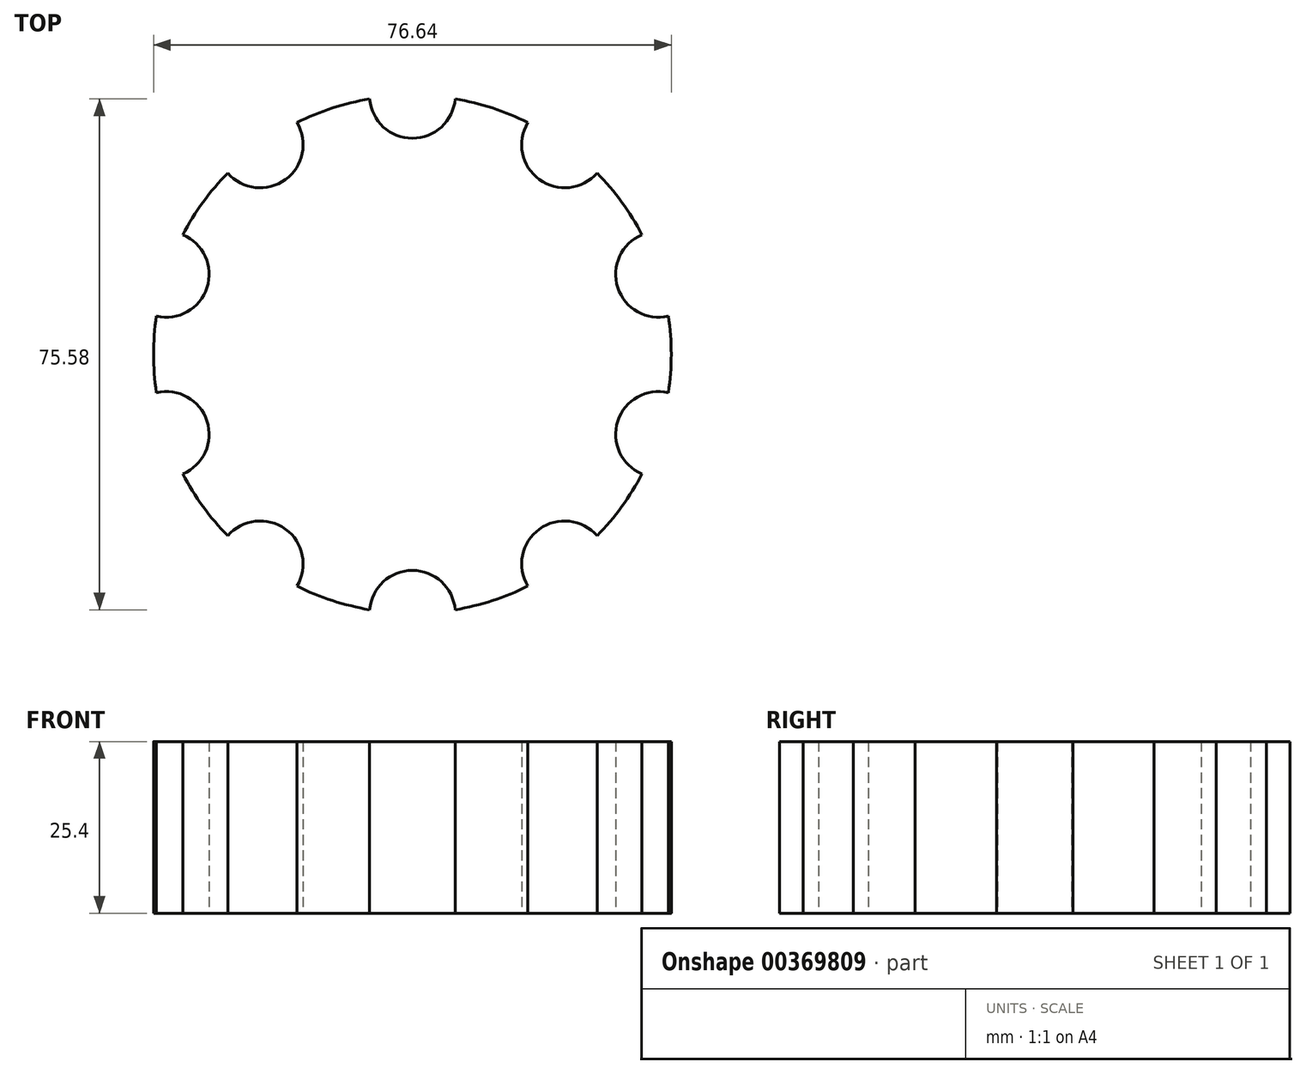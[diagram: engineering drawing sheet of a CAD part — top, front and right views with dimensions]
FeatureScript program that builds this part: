
annotation { "Feature Type Name" : "Feature", "Feature Type Description" : "" }
export const myFeature = defineFeature(function(context is Context, id is Id, definition is map)
    precondition{}
    {
        {
            var Q0;
            Q0=qCreatedBy(makeId("Top.planeOp"),FACE);
            var sketch = newSketch(context, id + "F0", { "sketchPlane" : qUnion([Q0])});
            skCircle(sketch, "E0", {"center": v(0, 0) * mm, "radius": 38.32 * mm});
            skCircle(sketch, "E1", {"center": v(0, 38.32) * mm, "radius": 6.35 * mm});
            skCircle(sketch, "E2.1.0", {"center": v(-22.52, 31) * mm, "radius": 6.35 * mm});
            skCircle(sketch, "E2.2.0", {"center": v(-36.44, 11.84) * mm, "radius": 6.35 * mm});
            skCircle(sketch, "E2.3.0", {"center": v(-36.44, -11.84) * mm, "radius": 6.35 * mm});
            skCircle(sketch, "E2.4.0", {"center": v(-22.52, -31) * mm, "radius": 6.35 * mm});
            skCircle(sketch, "E2.5.0", {"center": v(0, -38.32) * mm, "radius": 6.35 * mm});
            skCircle(sketch, "E2.6.0", {"center": v(22.52, -31) * mm, "radius": 6.35 * mm});
            skCircle(sketch, "E2.7.0", {"center": v(36.44, -11.84) * mm, "radius": 6.35 * mm});
            skCircle(sketch, "E2.8.0", {"center": v(36.44, 11.84) * mm, "radius": 6.35 * mm});
            skCircle(sketch, "E2.9.0", {"center": v(22.52, 31) * mm, "radius": 6.35 * mm});
            skSolve(sketch);
        }
        {
            var Q0;
            {var subQ0=sQuery(id+"F0.wireOp",EDGE,"E2.8.0");var subQ1=sQuery(id+"F0.wireOp",EDGE,"E0");var subQ17=makeQuery(id+"F0.imprint","INTERSECT",VERTEX,{"disambiguationData":[OD(0.0)],"derivedFrom":[subQ1,subQ0]});Q0=makeQuery(id+"F0.imprint","IMPRINT",FACE,{"disambiguationData":[TD([[makeQuery(id+"F0.imprint","IMPRINT",EDGE,{"disambiguationData":[TD([[subQ17,-1.0]])],"derivedFrom":subQ1}),1.0]])]});}
            extrude(context, id + "F1", {"entities" : qUnion([Q0]), "depth" : 25.4 * mm});
        }
    });
